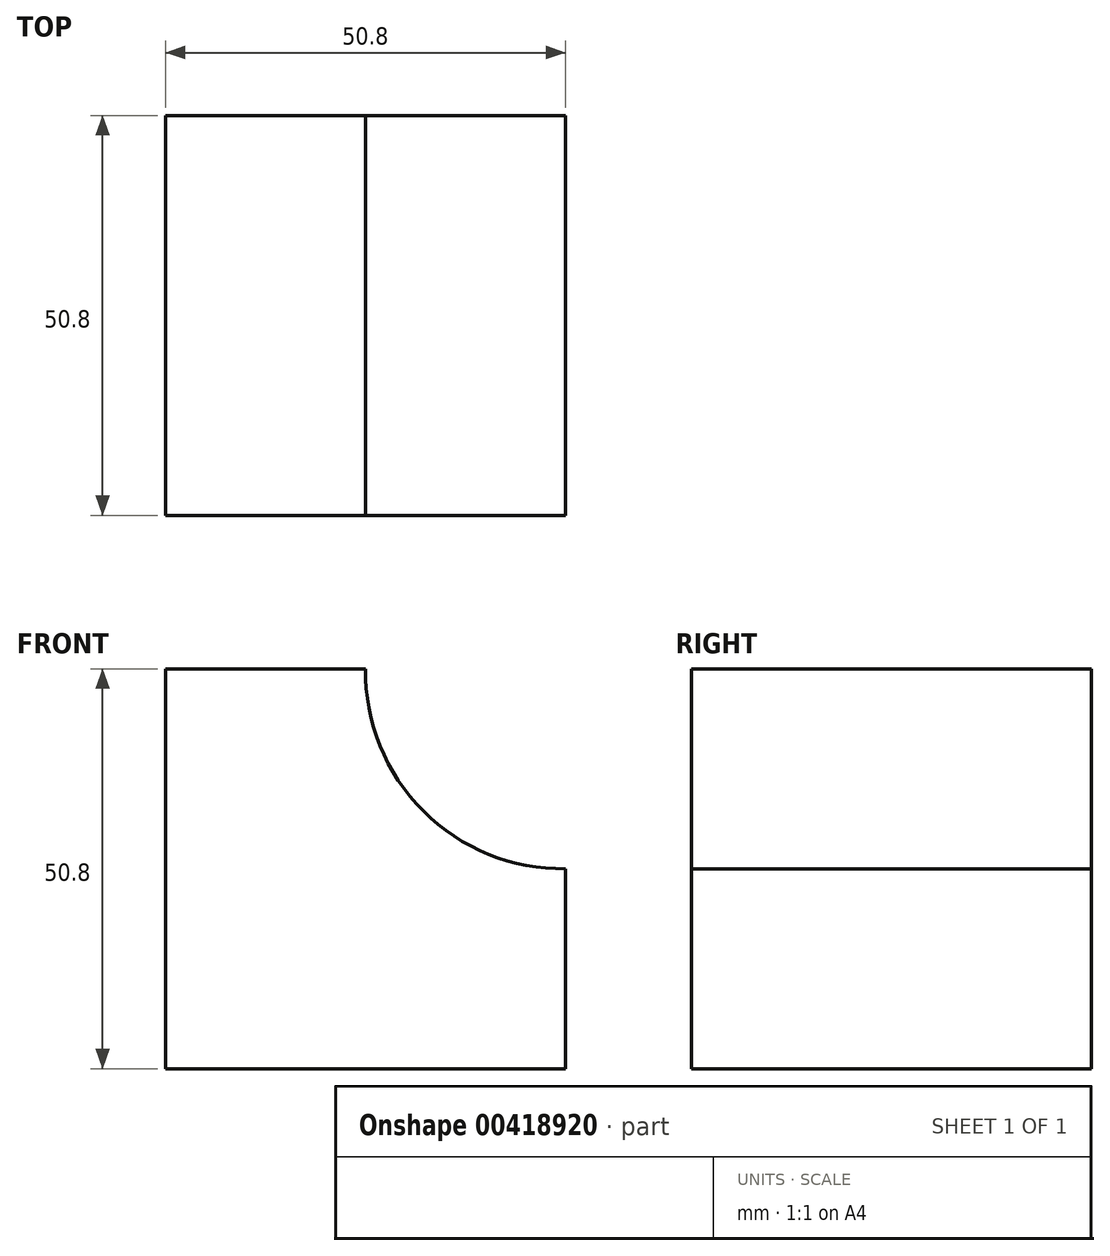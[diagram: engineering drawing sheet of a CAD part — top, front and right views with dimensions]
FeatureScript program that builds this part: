
annotation { "Feature Type Name" : "Feature", "Feature Type Description" : "" }
export const myFeature = defineFeature(function(context is Context, id is Id, definition is map)
    precondition{}
    {
        {
            var Q0;
            Q0=qCreatedBy(makeId("Front.planeOp"),FACE);
            var sketch = newSketch(context, id + "F0", { "sketchPlane" : qUnion([Q0])});
            skLineSegment(sketch, "E0", {"start": v(0, 0) * mm, "end": v(-50.8, 0) * mm});
            skLineSegment(sketch, "E1", {"start": v(-50.8, 0) * mm, "end": v(-50.8, 50.8) * mm});
            skLineSegment(sketch, "E2", {"start": v(-50.8, 50.8) * mm, "end": v(-25.4, 50.8) * mm});
            skLineSegment(sketch, "E3", {"start": v(0, 0) * mm, "end": v(0, 25.4) * mm});
            skArc(sketch, "E4", {"start": v(-25.4, 50.8) * mm, "mid": v(-18.07, 32.73) * mm, "end": v(0, 25.4) * mm});
            skSolve(sketch);
        }
        {
            var Q0;
            Q0=makeQuery(id+"F0.imprint","IMPRINT",FACE,{"disambiguationData":[TD([[makeQuery(id+"F0.imprint","IMPRINT",EDGE,{"derivedFrom":sQuery(id+"F0.wireOp",EDGE,"E0")}),-1.0]])]});
            extrude(context, id + "F1", {"entities" : qUnion([Q0]), "depth" : 50.8 * mm});
        }
    });
